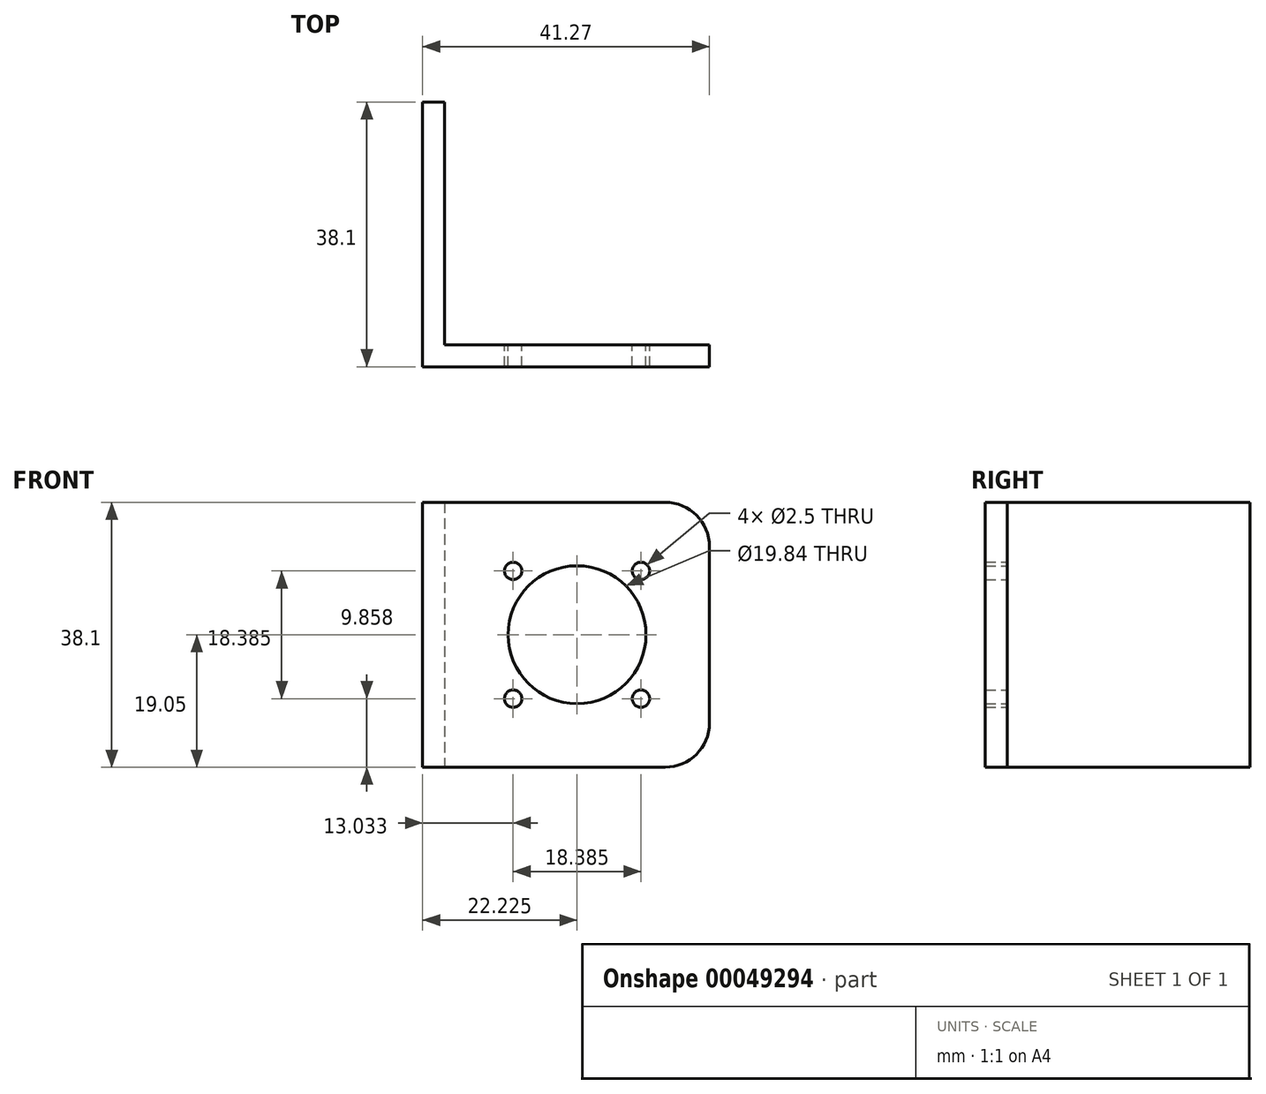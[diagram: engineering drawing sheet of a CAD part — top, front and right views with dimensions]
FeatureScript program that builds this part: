
annotation { "Feature Type Name" : "Feature", "Feature Type Description" : "" }
export const myFeature = defineFeature(function(context is Context, id is Id, definition is map)
    precondition{}
    {
        {
            var Q0;
            Q0=qCreatedBy(makeId("Top.planeOp"),FACE);
            var sketch = newSketch(context, id + "F0", { "sketchPlane" : qUnion([Q0])});
            skLineSegment(sketch, "E0", {"start": v(0, 0) * mm, "end": v(0, 38.1) * mm});
            skLineSegment(sketch, "E1", {"start": v(0, 38.1) * mm, "end": v(3.17, 38.1) * mm});
            skLineSegment(sketch, "E2", {"start": v(3.17, 38.1) * mm, "end": v(3.18, 3.17) * mm});
            skLineSegment(sketch, "E3", {"start": v(3.18, 3.17) * mm, "end": v(41.28, 3.18) * mm});
            skLineSegment(sketch, "E4", {"start": v(41.28, 3.18) * mm, "end": v(41.28, 0) * mm});
            skLineSegment(sketch, "E5", {"start": v(41.28, 0) * mm, "end": v(0, 0) * mm});
            skSolve(sketch);
        }
        {
            var Q0;
            Q0 = qSketchRegion(id + "F0", true);
            extrude(context, id + "F1", {"entities" : qUnion([Q0]), "depth" : 38.1 * mm});
        }
        {
            var Q0;
            Q0=makeQuery(id+"F1.opExtrude","SWEPT_FACE",FACE,{"disambiguationData":[OSD([sQuery(id+"F0.wireOp",EDGE,"E3")])]});
            var sketch = newSketch(context, id + "F2", { "sketchPlane" : qUnion([Q0])});
            skLineSegment(sketch, "E6", {"start": v(-3.17, 19.05) * mm, "end": v(-41.28, 19.05) * mm, "construction": true});
            skPoint(sketch, "E7.center", {"position": v(-22.23, 19.05) * mm});
            skLineSegment(sketch, "E8", {"start": v(-22.23, 28.08) * mm, "end": v(-22.23, 0) * mm, "construction": true});
            skCircle(sketch, "E9", {"center": v(-22.23, 19.05) * mm, "radius": 9.92 * mm});
            skCircle(sketch, "E10", {"center": v(-22.23, 19.05) * mm, "radius": 13 * mm, "construction": true});
            skLineSegment(sketch, "E11", {"start": v(-13.03, 28.24) * mm, "end": v(-22.23, 19.05) * mm, "construction": true});
            skCircle(sketch, "E7.3.0", {"center": v(-13.03, 9.86) * mm, "radius": 1.25 * mm});
            skCircle(sketch, "E7.1.0", {"center": v(-31.42, 28.24) * mm, "radius": 1.25 * mm});
            skCircle(sketch, "E7.2.0", {"center": v(-31.42, 9.86) * mm, "radius": 1.25 * mm});
            skCircle(sketch, "E12", {"center": v(-13.03, 28.24) * mm, "radius": 1.25 * mm});
            skSolve(sketch);
        }
        {
            var Q0;
            Q0 = qSketchRegion(id + "F2", true);
            extrude(context, id + "F3", {"entities" : qUnion([Q0]), "operationType" : NewBodyOperationType.REMOVE, "endBound" : BoundingType.UP_TO_NEXT, "oppositeDirection" : true, "depth" : 25.4 * mm});
        }
        {
            var Q0;
            Q0=makeQuery(id+"F1.opExtrude","CAP_EDGE",EDGE,{"disambiguationData":[OSD([sQuery(id+"F0.wireOp",EDGE,"E4")])],"isStart":false});
            var Q1;
            Q1=makeQuery(id+"F1.opExtrude","CAP_EDGE",EDGE,{"disambiguationData":[OSD([sQuery(id+"F0.wireOp",EDGE,"E4")])],"isStart":true});
            fillet(context, id + "F4", {"entities" : qUnion([Q0, Q1]), "radius" : 6.35 * mm, "tangentPropagation" : true, "allowEdgeOverflow" : false});
        }
    });
